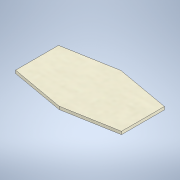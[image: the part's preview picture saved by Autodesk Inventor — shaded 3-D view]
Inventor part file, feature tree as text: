
AUTODESK INVENTOR PART (.ipt)
format: ipt  version: 2021 (Build 250183000, 183)  size: 102,912 bytes
history: native  units: mm
features: extrude x1, sketch x1
ambient origin geometry x8: Origin, YZ Plane, XZ Plane, XY Plane, X Axis, Y Axis, Z Axis, Center Point
bodies: Solid1 (feature_tree)
feature tree (2):
  extrude  "Extrusion1"  Depth=1.7mm
  sketch  "Sketch1"  dims[d0=61.7mm d1=25.0mm d2=36.0mm d3=1.7mm d4=0.0mm]
